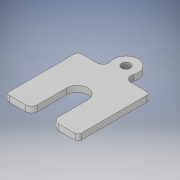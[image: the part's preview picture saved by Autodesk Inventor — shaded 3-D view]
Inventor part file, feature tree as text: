
AUTODESK INVENTOR PART (.ipt)
format: ipt  version: 2018 (Build 220112000, 112)  size: 140,800 bytes
history: native  units: in
note: dims shown in document units (in); Inventor stores cm internally (conversion verified against a paired STEP export)
features: extrude x1, sketch x1, fillet x1
ambient origin geometry x8: Origin, YZ Plane, XZ Plane, XY Plane, X Axis, Y Axis, Z Axis, Center Point
bodies: Solid1 (feature_tree)
feature tree (3):
  extrude  "Extrusion1"  Depth=1.0in TaperAngle=0.0deg
  sketch  "Sketch1"  dims[d0=0.183in d1=1.0in d2=0.0in]
  fillet  "Fillet2"  [1 undecoded]
note: 1 required parameter value undecoded (feature->parameter linkage not recoverable at this tier; creation-order binding heuristic only, values carry confidence <= 0.55)
